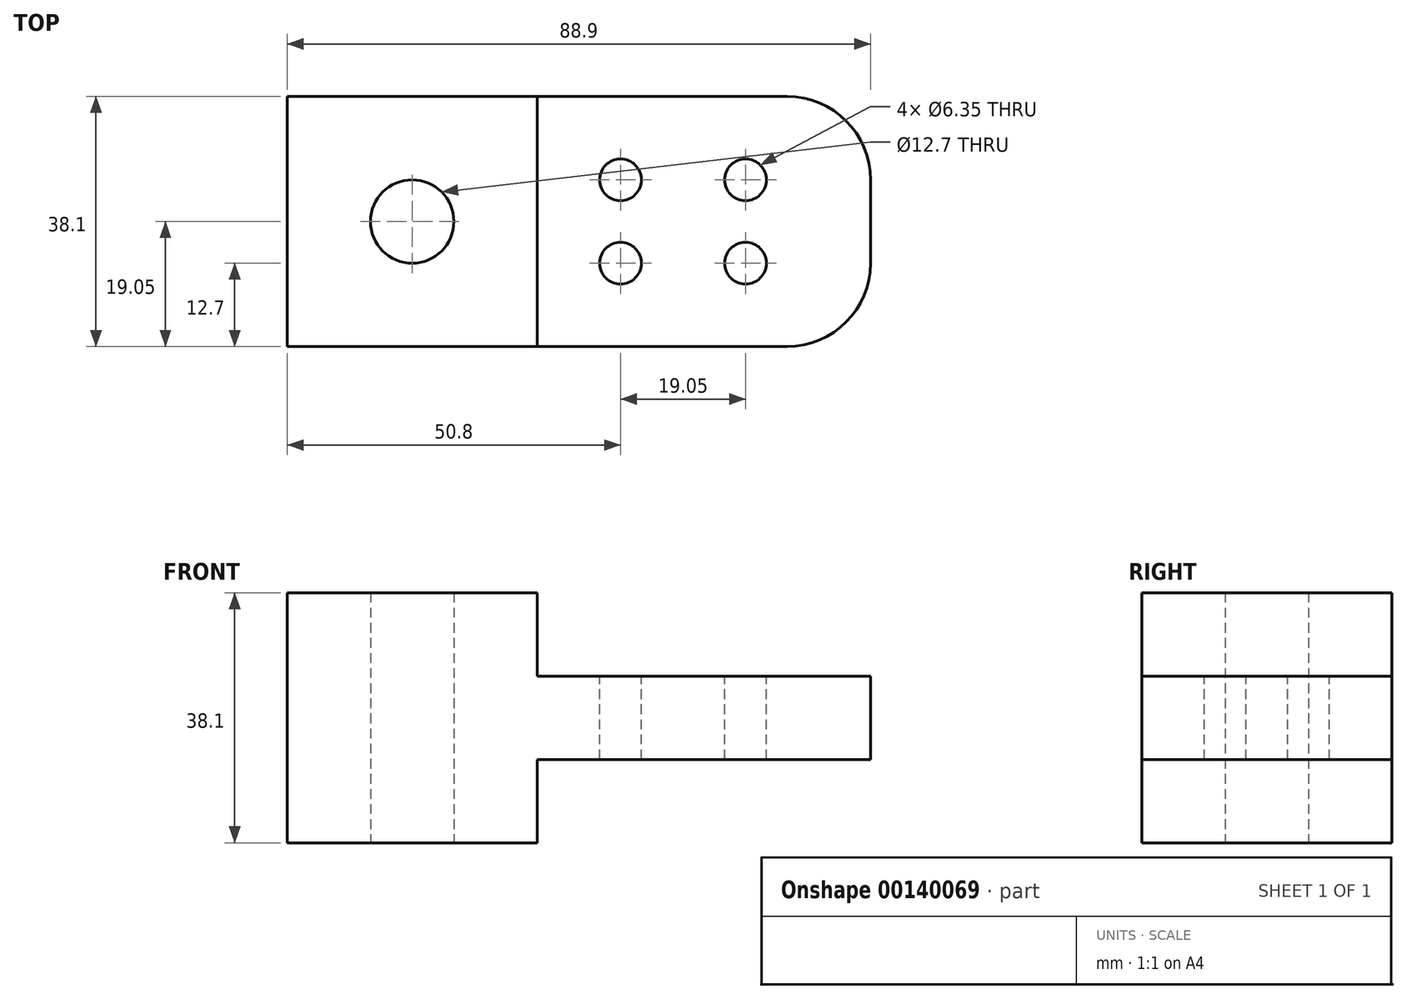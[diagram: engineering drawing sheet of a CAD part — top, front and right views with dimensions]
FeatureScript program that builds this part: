
annotation { "Feature Type Name" : "Feature", "Feature Type Description" : "" }
export const myFeature = defineFeature(function(context is Context, id is Id, definition is map)
    precondition{}
    {
        {
            var Q0;
            Q0=qCreatedBy(makeId("Top.planeOp"),FACE);
            var sketch = newSketch(context, id + "F0", { "sketchPlane" : qUnion([Q0])});
            skLineSegment(sketch, "E0.bottom", {"start": v(0, 0) * mm, "end": v(38.1, 0) * mm});
            skLineSegment(sketch, "E0.top", {"start": v(0, 38.1) * mm, "end": v(38.1, 38.1) * mm});
            skLineSegment(sketch, "E0.left", {"start": v(0, 0) * mm, "end": v(0, 38.1) * mm});
            skLineSegment(sketch, "E0.right", {"start": v(38.1, 0) * mm, "end": v(38.1, 38.1) * mm});
            skCircle(sketch, "E1", {"center": v(19.05, 19.05) * mm, "radius": 6.35 * mm});
            skSolve(sketch);
        }
        {
            var Q0;
            Q0 = qSketchRegion(id + "F0", true);
            extrude(context, id + "F1", {"entities" : qUnion([Q0]), "depth" : 38.1 * mm});
        }
        {
            var Q0;
            Q0=makeQuery(id+"F1.opExtrude","SWEPT_FACE",FACE,{"disambiguationData":[OSD([sQuery(id+"F0.wireOp",EDGE,"E0.right")])]});
            var sketch = newSketch(context, id + "F2", { "sketchPlane" : qUnion([Q0])});
            skLineSegment(sketch, "E2.bottom", {"start": v(0, 25.4) * mm, "end": v(38.1, 25.4) * mm});
            skLineSegment(sketch, "E2.top", {"start": v(0, 12.7) * mm, "end": v(38.1, 12.7) * mm});
            skLineSegment(sketch, "E2.left", {"start": v(0, 25.4) * mm, "end": v(0, 12.7) * mm});
            skLineSegment(sketch, "E2.right", {"start": v(38.1, 25.4) * mm, "end": v(38.1, 12.7) * mm});
            skSolve(sketch);
        }
        {
            var Q0;
            Q0 = qSketchRegion(id + "F2", true);
            extrude(context, id + "F3", {"entities" : qUnion([Q0]), "operationType" : NewBodyOperationType.ADD, "depth" : 50.8 * mm});
        }
        {
            var Q0;
            Q0=makeQuery(id+"F3.opExtrude","CAP_EDGE",EDGE,{"disambiguationData":[OSD([sQuery(id+"F2.wireOp",EDGE,"E2.right")])],"isStart":false});
            fillet(context, id + "F4", {"entities" : qUnion([Q0]), "radius" : 12.7 * mm, "tangentPropagation" : true, "allowEdgeOverflow" : false});
        }
        {
            var Q0;
            Q0=makeQuery(id+"F3.opExtrude","CAP_EDGE",EDGE,{"disambiguationData":[OSD([sQuery(id+"F2.wireOp",EDGE,"E2.left")])],"isStart":false});
            fillet(context, id + "F5", {"entities" : qUnion([Q0]), "radius" : 12.7 * mm, "tangentPropagation" : true, "allowEdgeOverflow" : false});
        }
        {
            var Q0;
            Q0=makeQuery(id+"F3.opExtrude","SWEPT_FACE",FACE,{"disambiguationData":[OSD([sQuery(id+"F2.wireOp",EDGE,"E2.bottom")])]});
            var sketch = newSketch(context, id + "F6", { "sketchPlane" : qUnion([Q0])});
            skCircle(sketch, "E3", {"center": v(50.8, 25.4) * mm, "radius": 3.18 * mm});
            skCircle(sketch, "E4", {"center": v(69.85, 25.4) * mm, "radius": 3.18 * mm});
            skCircle(sketch, "E5", {"center": v(50.8, 12.7) * mm, "radius": 3.18 * mm});
            skCircle(sketch, "E6", {"center": v(69.85, 12.7) * mm, "radius": 3.18 * mm});
            skSolve(sketch);
        }
        {
            var Q0;
            Q0 = qSketchRegion(id + "F6", true);
            extrude(context, id + "F7", {"entities" : qUnion([Q0]), "operationType" : NewBodyOperationType.REMOVE, "endBound" : BoundingType.THROUGH_ALL, "oppositeDirection" : true, "depth" : 25.4 * mm});
        }
    });
